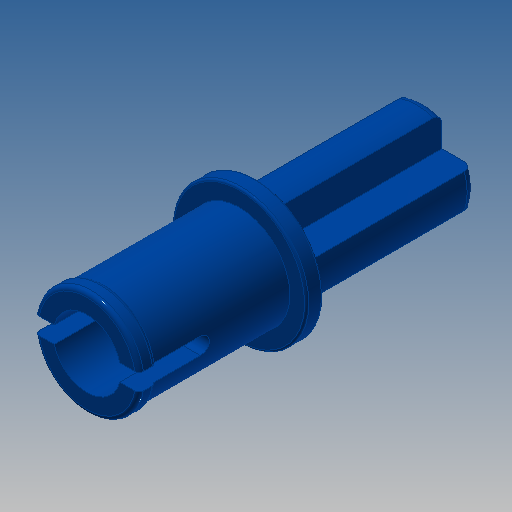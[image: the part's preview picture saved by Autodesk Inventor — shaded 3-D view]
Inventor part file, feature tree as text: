
AUTODESK INVENTOR PART (.ipt)
format: ipt  version: 2022.2 (Build 262287000, 287)  size: 262,144 bytes
history: native  units: mm (DEFAULTED — no unit token found)
features: sketch x3, fillet x2, extrude x2, revolve x1
ambient origin geometry x8: Origin, YZ Plane, XZ Plane, XY Plane, X Axis, Y Axis, Z Axis, Center Point
bodies: Solid2 (feature_tree)
feature tree (8):
  revolve  "Revolution1"  [1 undecoded]
  fillet  "Fillet1"  Radius=0.75mm
  extrude  "Extrusion2"  Depth=8.0mm
  extrude  "Extrusion3"  Depth=0.4mm
  fillet  "Fillet2"  [1 undecoded]
  sketch  "Sketch1"  dims[d1=4.8mm d2=5.0mm d4=0.75mm]
  sketch  "Sketch2"  dims[d6=8.0mm d7=0.8mm]
  sketch  "Sketch3"  dims[d8=6.4mm d9=0.8mm d10=0.0mm d19=8.0mm d20=90.0deg d25=10.0mm d26=0.0mm d27=0.2mm d28=0.1mm d30=0.0mm d34=3.4mm d35=4.8mm d36=1.6mm d37=8.0mm d38=0.0mm d39=0.4mm d40=3.2mm d41=0.8mm d42=0.0mm d43=0.0mm]
note: 2 required parameter values undecoded (feature->parameter linkage not recoverable at this tier; creation-order binding heuristic only, values carry confidence <= 0.55)